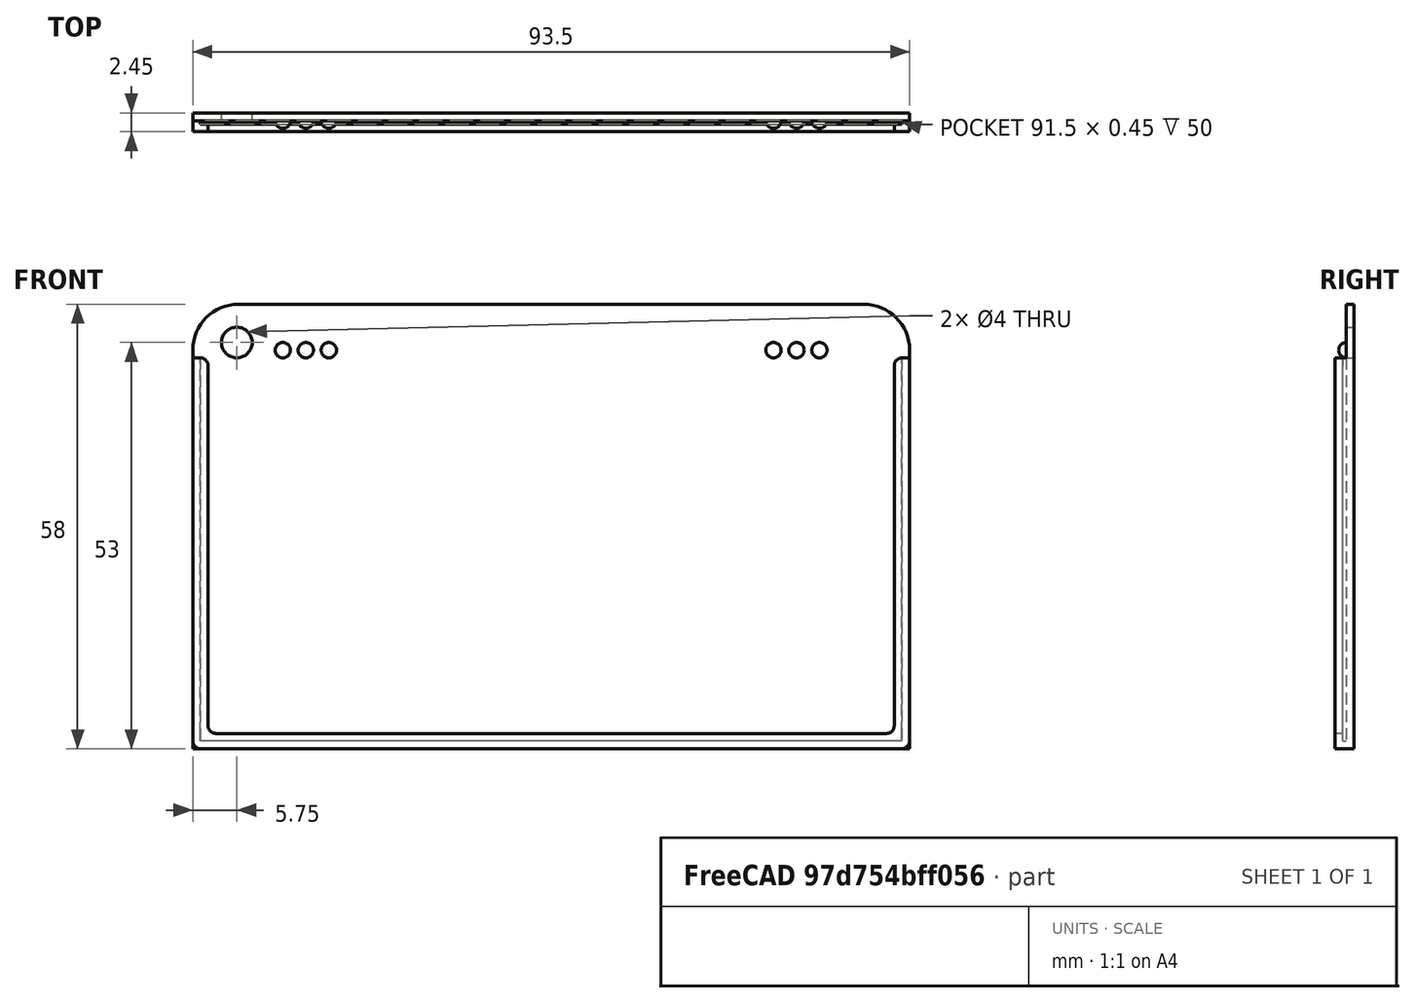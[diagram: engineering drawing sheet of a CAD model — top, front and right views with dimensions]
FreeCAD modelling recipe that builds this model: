
FCSTD DOCUMENT  (FreeCAD 0.18R16146 (Git))
Label: dog-card
License: All rights reserved
LicenseURL: http://en.wikipedia.org/wiki/All_rights_reserved
objects: Part::Box×7, Part::Sphere×6, Part::MultiFuse×3, Part::Fillet×3, Part::Cylinder×1, Part::Cut×1, Part::Feature×1
note: 22 computed .brp shape members not serialized (recipe doc carries the construction recipe); baked Part::Feature solids carry a one-line shape summary decoded from their .brp

FEATURE [Part::Box] Box  label="Cube"
  AttacherType = Attacher::AttachEngine3D
  Height = 1
  Length = 93.5
  Placement = pos=(-46.75,0,0) rot=(0,0,1;0rad)
  Width = 2.45
FEATURE [Part::Box] Box001  label="Cube001"
  AttacherType = Attacher::AttachEngine3D
  Height = 58
  Length = 93.5
  Placement = pos=(-46.75,1.45,0) rot=(0,0,1;0rad)
  Width = 1
FEATURE [Part::Box] Box002  label="Cube002"
  AttacherType = Attacher::AttachEngine3D
  Height = 51
  Length = 2
  Placement = pos=(-46.75,0,0) rot=(0,0,1;0rad)
  Width = 1
FEATURE [Part::Box] Box003  label="Cube003"
  AttacherType = Attacher::AttachEngine3D
  Height = 51
  Length = 1
  Placement = pos=(-46.75,0,0) rot=(0,0,1;0rad)
  Width = 2.45
FEATURE [Part::Box] Box004  label="Cube004"
  AttacherType = Attacher::AttachEngine3D
  Height = 51
  Length = 1
  Placement = pos=(45.75,0,0) rot=(0,0,1;0rad)
  Width = 2.45
FEATURE [Part::Box] Box005  label="Cube005"
  AttacherType = Attacher::AttachEngine3D
  Height = 51
  Length = 2
  Placement = pos=(44.75,0,0) rot=(0,0,1;0rad)
  Width = 1
FEATURE [Part::Box] Box006  label="Cube006"
  AttacherType = Attacher::AttachEngine3D
  Height = 2
  Length = 93.5
  Placement = pos=(-46.75,0,0) rot=(0,0,1;0rad)
  Width = 1
FEATURE [Part::MultiFuse] Fusion
  Shapes = -> [Box002,Box006,Box005]
FEATURE [Part::Fillet] Fillet
  Base = -> Fusion
  Edges = 4 edges r=1: [Edge21,Edge30,Edge31,Edge40]
FEATURE [Part::Cylinder] Cylinder
  Angle = 360
  AttacherType = Attacher::AttachEngine3D
  Height = 10
  Placement = pos=(-41,-4,53) rot=(1,0,0;4.71239rad)
  Radius = 2
FEATURE [Part::Fillet] Fillet001
  Base = -> Box001
  Edges = 2 edges r=6: [Edge2,Edge6]
FEATURE [Part::Cut] Cut
  Base = -> Fillet001
  Tool = -> Cylinder
FEATURE [Part::MultiFuse] Fusion001
  Shapes = -> [Box,Cut,Box003,Box004,Fillet]
FEATURE [Part::Feature] Fusion001001  label="Fusion002"
  shape: bbox 93.5 x 2.45 x 58 mm, 23 faces (baked)
FEATURE [Part::Fillet] Fillet002
  Base = -> Fusion001001
  Edges = 2 edges r=1: [Edge57,Edge59]
FEATURE [Part::Sphere] Sphere
  Angle1 = -90
  Angle2 = 90
  Angle3 = 360
  AttacherType = Attacher::AttachEngine3D
  Placement = pos=(-35,1.45,52) rot=(0,0,1;0rad)
  Radius = 1
FEATURE [Part::Sphere] Sphere001
  Angle1 = -90
  Angle2 = 90
  Angle3 = 360
  AttacherType = Attacher::AttachEngine3D
  Placement = pos=(35,1.45,52) rot=(0,0,1;0rad)
  Radius = 1
FEATURE [Part::Sphere] Sphere002
  Angle1 = -90
  Angle2 = 90
  Angle3 = 360
  AttacherType = Attacher::AttachEngine3D
  Placement = pos=(32,1.45,52) rot=(0,0,1;0rad)
  Radius = 1
FEATURE [Part::Sphere] Sphere003
  Angle1 = -90
  Angle2 = 90
  Angle3 = 360
  AttacherType = Attacher::AttachEngine3D
  Placement = pos=(-32,1.45,52) rot=(0,0,1;0rad)
  Radius = 1
FEATURE [Part::Sphere] Sphere004
  Angle1 = -90
  Angle2 = 90
  Angle3 = 360
  AttacherType = Attacher::AttachEngine3D
  Placement = pos=(-29,1.45,52) rot=(0,0,1;0rad)
  Radius = 1
FEATURE [Part::Sphere] Sphere005
  Angle1 = -90
  Angle2 = 90
  Angle3 = 360
  AttacherType = Attacher::AttachEngine3D
  Placement = pos=(29,1.45,52) rot=(0,0,1;0rad)
  Radius = 1
FEATURE [Part::MultiFuse] Fusion001002
  Shapes = -> [Sphere005,Sphere004,Sphere003,Sphere002,Sphere001,Sphere,Fillet002]
